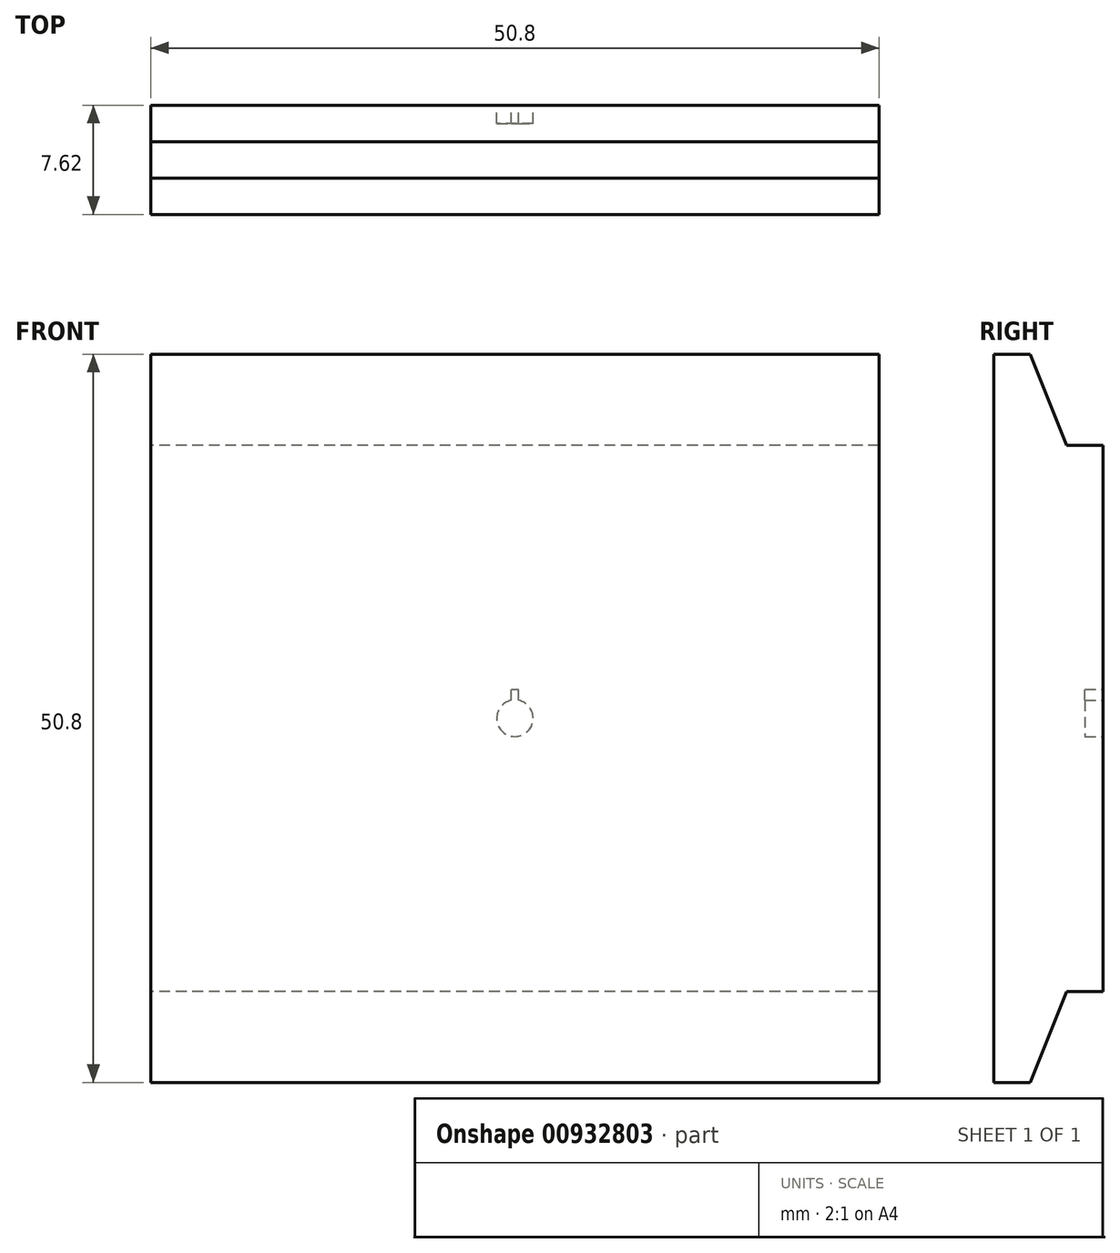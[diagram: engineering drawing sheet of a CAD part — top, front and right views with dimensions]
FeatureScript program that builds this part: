
annotation { "Feature Type Name" : "Feature", "Feature Type Description" : "" }
export const myFeature = defineFeature(function(context is Context, id is Id, definition is map)
    precondition{}
    {
        {
            var Q0;
            Q0=qCreatedBy(makeId("Right.planeOp"),FACE);
            var sketch = newSketch(context, id + "F0", { "sketchPlane" : qUnion([Q0])});
            skLineSegment(sketch, "E0", {"start": v(0, 0) * mm, "end": v(0, 19.05) * mm});
            skLineSegment(sketch, "E1", {"start": v(0, 19.05) * mm, "end": v(-2.54, 19.05) * mm});
            skLineSegment(sketch, "E2", {"start": v(-2.54, 19.05) * mm, "end": v(-5.08, 25.4) * mm});
            skLineSegment(sketch, "E3", {"start": v(-5.08, 25.4) * mm, "end": v(-7.62, 25.4) * mm});
            skLineSegment(sketch, "E4", {"start": v(-7.62, 25.4) * mm, "end": v(-7.62, -25.4) * mm});
            skLineSegment(sketch, "E5", {"start": v(-7.62, -25.4) * mm, "end": v(-5.08, -25.4) * mm});
            skLineSegment(sketch, "E6", {"start": v(-5.08, -25.4) * mm, "end": v(-2.54, -19.05) * mm});
            skLineSegment(sketch, "E7", {"start": v(-2.54, -19.05) * mm, "end": v(0, -19.05) * mm});
            skLineSegment(sketch, "E8", {"start": v(0, -19.05) * mm, "end": v(0, 0) * mm});
            skSolve(sketch);
        }
        {
            var Q0;
            Q0 = qSketchRegion(id + "F0", true);
            extrude(context, id + "F1", {"entities" : qUnion([Q0]), "depth" : 25.4 * mm, "offsetDistance" : 25.4 * mm});
        }
        {
            var Q0;
            Q0 = qSketchRegion(id + "F0", true);
            extrude(context, id + "F2", {"entities" : qUnion([Q0]), "operationType" : NewBodyOperationType.ADD, "oppositeDirection" : true, "depth" : 25.4 * mm, "offsetDistance" : 25.4 * mm});
        }
        {
            var Q0;
            Q0=makeQuery(id+"F1.opExtrude","SWEPT_FACE",FACE,{"disambiguationData":[OSD([sQuery(id+"F0.wireOp",EDGE,"E0"),sQuery(id+"F0.wireOp",EDGE,"E8")])]});
            var sketch = newSketch(context, id + "F3", { "sketchPlane" : qUnion([Q0])});
            skCircle(sketch, "E9", {"center": v(0, 0) * mm, "radius": 1.27 * mm});
            skLineSegment(sketch, "E10.bottom", {"start": v(0.25, 1.02) * mm, "end": v(-0.25, 1.02) * mm});
            skLineSegment(sketch, "E10.top", {"start": v(0.25, 2.03) * mm, "end": v(-0.25, 2.03) * mm});
            skLineSegment(sketch, "E10.left", {"start": v(0.25, 1.02) * mm, "end": v(0.25, 2.03) * mm});
            skLineSegment(sketch, "E10.right", {"start": v(-0.25, 1.02) * mm, "end": v(-0.25, 2.03) * mm});
            skPoint(sketch, "E10.middle", {"position": v(0, 1.52) * mm});
            skSolve(sketch);
        }
        {
            var Q0;
            Q0 = qSketchRegion(id + "F3", true);
            extrude(context, id + "F4", {"entities" : qUnion([Q0]), "operationType" : NewBodyOperationType.REMOVE, "oppositeDirection" : true, "depth" : 1.27 * mm, "offsetDistance" : 25.4 * mm});
        }
    });
